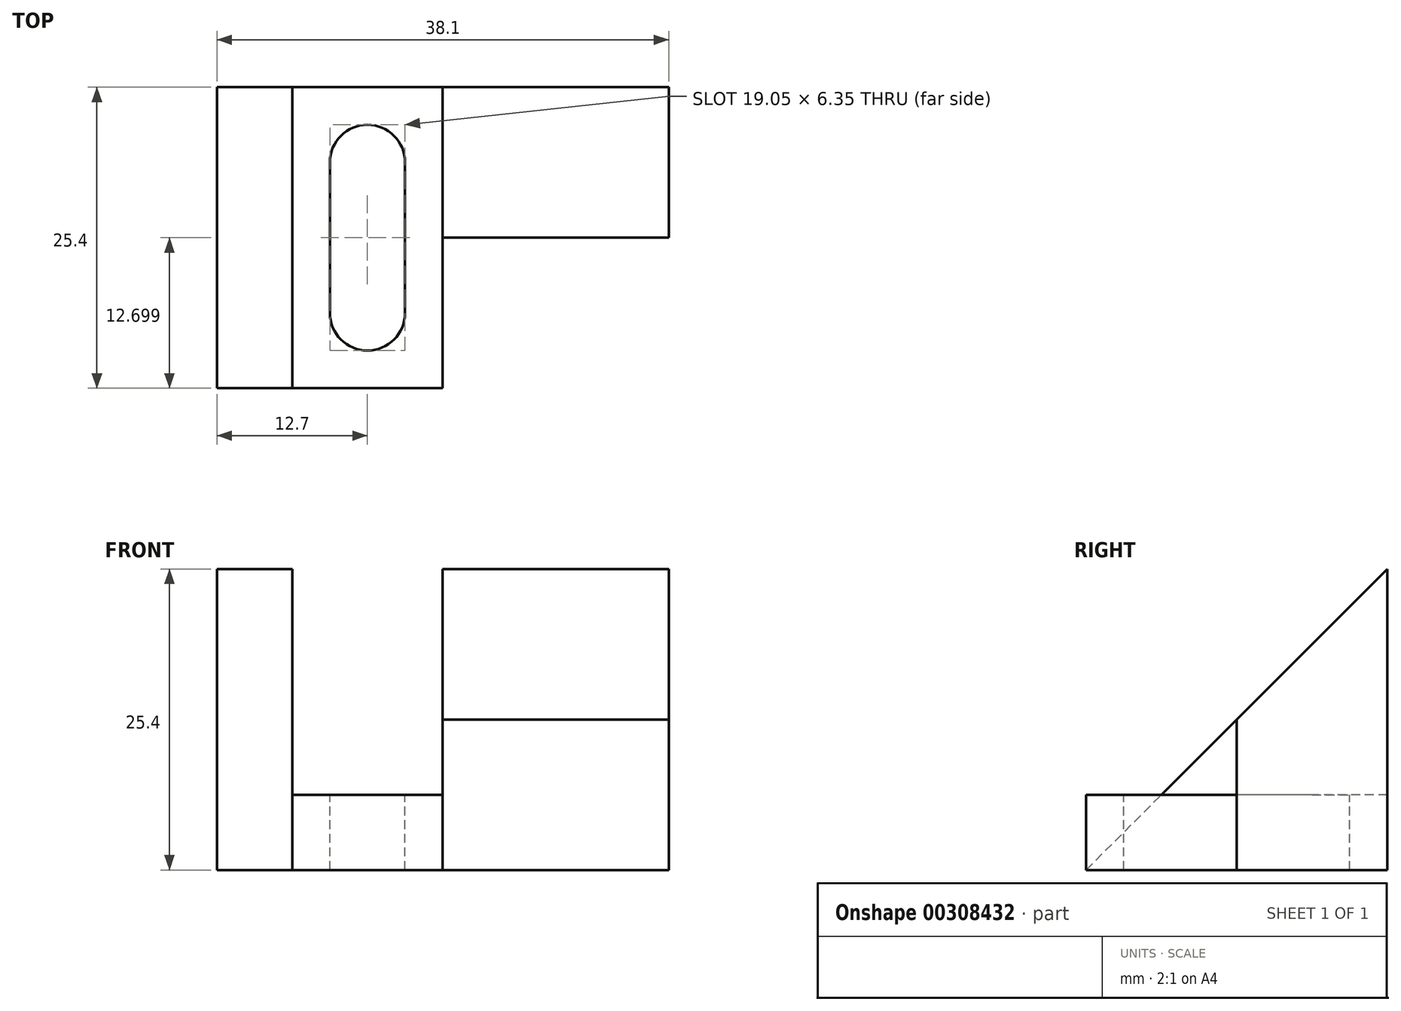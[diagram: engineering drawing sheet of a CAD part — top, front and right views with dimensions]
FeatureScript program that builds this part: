
annotation { "Feature Type Name" : "Feature", "Feature Type Description" : "" }
export const myFeature = defineFeature(function(context is Context, id is Id, definition is map)
    precondition{}
    {
        {
            var Q0;
            Q0=qCreatedBy(makeId("Front.planeOp"),FACE);
            var sketch = newSketch(context, id + "F0", { "sketchPlane" : qUnion([Q0])});
            skLineSegment(sketch, "E0", {"start": v(0, 0) * mm, "end": v(0, 25.4) * mm});
            skLineSegment(sketch, "E1", {"start": v(0, 25.4) * mm, "end": v(6.35, 25.4) * mm});
            skLineSegment(sketch, "E2", {"start": v(6.35, 25.4) * mm, "end": v(6.35, 0) * mm});
            skLineSegment(sketch, "E3", {"start": v(6.35, 0) * mm, "end": v(0, 0) * mm});
            skSolve(sketch);
        }
        {
            var Q0;
            Q0 = qSketchRegion(id + "F0", true);
            extrude(context, id + "F1", {"entities" : qUnion([Q0]), "endBound" : BoundingType.SYMMETRIC, "depth" : 25.4 * mm});
        }
        {
            var Q0;
            Q0=makeQuery(id+"F1.opExtrude","CAP_FACE",FACE,{"disambiguationData":[OSD([sQuery(id+"F0.wireOp",EDGE,"E0"),sQuery(id+"F0.wireOp",EDGE,"E1"),sQuery(id+"F0.wireOp",EDGE,"E2"),sQuery(id+"F0.wireOp",EDGE,"E3")])],"isStart":false});
            var sketch = newSketch(context, id + "F2", { "sketchPlane" : qUnion([Q0])});
            skLineSegment(sketch, "E4", {"start": v(6.35, 0) * mm, "end": v(19.05, 0) * mm});
            skLineSegment(sketch, "E5", {"start": v(19.05, 0) * mm, "end": v(19.05, 6.35) * mm});
            skLineSegment(sketch, "E6", {"start": v(19.05, 6.35) * mm, "end": v(6.35, 6.35) * mm});
            skLineSegment(sketch, "E7", {"start": v(6.35, 6.35) * mm, "end": v(6.35, 0) * mm});
            skSolve(sketch);
        }
        {
            var Q0;
            Q0 = qSketchRegion(id + "F2", true);
            extrude(context, id + "F3", {"entities" : qUnion([Q0]), "operationType" : NewBodyOperationType.ADD, "oppositeDirection" : true, "depth" : 25.4 * mm});
        }
        {
            var Q0;
            Q0=makeQuery(id+"F3.boolean.opBoolean","MERGE",FACE,{"derivedFrom":[makeQuery(id+"F1.opExtrude","CAP_FACE",FACE,{"disambiguationData":[OSD([sQuery(id+"F0.wireOp",EDGE,"E0"),sQuery(id+"F0.wireOp",EDGE,"E1"),sQuery(id+"F0.wireOp",EDGE,"E2"),sQuery(id+"F0.wireOp",EDGE,"E3")])],"isStart":true}),makeQuery(id+"F3.opExtrude","CAP_FACE",FACE,{"disambiguationData":[OSD([sQuery(id+"F2.wireOp",EDGE,"E4"),sQuery(id+"F2.wireOp",EDGE,"E5"),sQuery(id+"F2.wireOp",EDGE,"E6"),sQuery(id+"F2.wireOp",EDGE,"E7")])],"isStart":false})]});
            var sketch = newSketch(context, id + "F4", { "sketchPlane" : qUnion([Q0])});
            skLineSegment(sketch, "E8", {"start": v(-19.05, 0) * mm, "end": v(-38.1, 0) * mm});
            skLineSegment(sketch, "E9", {"start": v(-38.1, 0) * mm, "end": v(-38.1, 12.7) * mm});
            skLineSegment(sketch, "E10", {"start": v(-38.1, 12.7) * mm, "end": v(-19.05, 12.7) * mm});
            skLineSegment(sketch, "E11", {"start": v(-19.05, 12.7) * mm, "end": v(-19.05, 0) * mm});
            skSolve(sketch);
        }
        {
            var Q0;
            Q0 = qSketchRegion(id + "F4", true);
            extrude(context, id + "F5", {"entities" : qUnion([Q0]), "operationType" : NewBodyOperationType.ADD, "oppositeDirection" : true, "depth" : 12.7 * mm});
        }
        {
            var Q0;
            Q0=makeQuery(id+"F5.opExtrude","SWEPT_FACE",FACE,{"disambiguationData":[OSD([sQuery(id+"F4.wireOp",EDGE,"E9")])]});
            var sketch = newSketch(context, id + "F6", { "sketchPlane" : qUnion([Q0])});
            skLineSegment(sketch, "E12", {"start": v(12.7, 12.7) * mm, "end": v(12.7, 25.4) * mm});
            skLineSegment(sketch, "E13", {"start": v(12.7, 25.4) * mm, "end": v(0, 12.7) * mm});
            skLineSegment(sketch, "E14", {"start": v(0, 12.7) * mm, "end": v(12.7, 12.7) * mm});
            skSolve(sketch);
        }
        {
            var Q0;
            Q0 = qSketchRegion(id + "F6", true);
            extrude(context, id + "F7", {"entities" : qUnion([Q0]), "operationType" : NewBodyOperationType.ADD, "oppositeDirection" : true, "depth" : 19.05 * mm});
        }
        {
            var Q0;
            Q0=makeQuery(id+"F1.opExtrude","SWEPT_FACE",FACE,{"disambiguationData":[OSD([sQuery(id+"F0.wireOp",EDGE,"E0")])]});
            var sketch = newSketch(context, id + "F8", { "sketchPlane" : qUnion([Q0])});
            skLineSegment(sketch, "E15", {"start": v(12.7, 0) * mm, "end": v(-12.7, 25.4) * mm});
            skLineSegment(sketch, "E16", {"start": v(-12.7, 25.4) * mm, "end": v(12.7, 25.4) * mm});
            skLineSegment(sketch, "E17", {"start": v(12.7, 25.4) * mm, "end": v(12.7, 0) * mm});
            skSolve(sketch);
        }
        {
            var Q0;
            Q0 = qSketchRegion(id + "F8", true);
            extrude(context, id + "F9", {"entities" : qUnion([Q0]), "operationType" : NewBodyOperationType.REMOVE, "oppositeDirection" : true, "depth" : 6.35 * mm});
        }
        {
            var Q0;
            Q0=makeQuery(id+"F3.opExtrude","SWEPT_FACE",FACE,{"disambiguationData":[OSD([sQuery(id+"F2.wireOp",EDGE,"E6")])]});
            var sketch = newSketch(context, id + "F10", { "sketchPlane" : qUnion([Q0])});
            skLineSegment(sketch, "E18", {"start": v(6.35, 12.7) * mm, "end": v(6.35, 6.35) * mm, "construction": true});
            skLineSegment(sketch, "E19", {"start": v(9.53, 6.35) * mm, "end": v(9.53, -6.35) * mm});
            skLineSegment(sketch, "E20", {"start": v(9.53, -6.35) * mm, "end": v(15.88, -6.35) * mm});
            skLineSegment(sketch, "E21", {"start": v(15.88, -6.35) * mm, "end": v(15.87, 6.35) * mm});
            skLineSegment(sketch, "E22", {"start": v(15.88, 6.35) * mm, "end": v(9.53, 6.35) * mm});
            skArc(sketch, "E23", {"start": v(9.53, -6.35) * mm, "mid": v(12.7, -9.52) * mm, "end": v(15.88, -6.35) * mm});
            skArc(sketch, "E24", {"start": v(15.87, 6.35) * mm, "mid": v(12.7, 9.52) * mm, "end": v(9.52, 6.35) * mm});
            skSolve(sketch);
        }
        {
            var Q0;
            Q0 = qSketchRegion(id + "F10", true);
            extrude(context, id + "F11", {"entities" : qUnion([Q0]), "operationType" : NewBodyOperationType.REMOVE, "oppositeDirection" : true, "depth" : 25.4 * mm});
        }
    });
